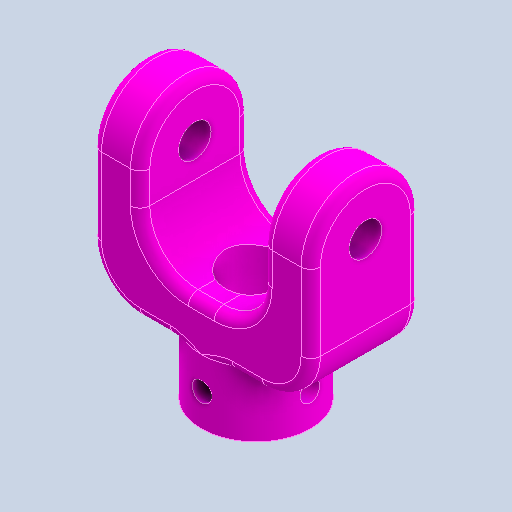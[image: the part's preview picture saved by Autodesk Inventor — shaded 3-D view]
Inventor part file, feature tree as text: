
AUTODESK INVENTOR PART (.ipt)
format: ipt  version: 2022 (Build 260153000, 153)  size: 330,752 bytes
history: native  units: in
note: dims shown in document units (in); Inventor stores cm internally (conversion verified against a paired STEP export)
features: extrude x5, sketch x5, fillet x4, plane x1, other x1, pattern_circular x1
ambient origin geometry x8: Origin, YZ Plane, XZ Plane, XY Plane, X Axis, Y Axis, Z Axis, Center Point
bodies: Solid1 (feature_tree)
feature tree (17):
  extrude  "Extrusion1"  Depth=2.6772in
  fillet  "Fillet1"  Radius=0.5906in
  fillet  "Fillet2"  Radius=0.5906in
  fillet  "Fillet3"  Radius=0.5512in
  extrude  "Extrusion2"  Depth=1.3386in TaperAngle=0.0deg
  extrude  "Extrusion3"  Depth=0.6693in
  fillet  "Fillet4"  Radius=0.5906in
  plane  "Work Plane1"
  extrude  "Extrusion4"  Depth=0.6693in
  other  "Work Axis1"
  pattern_circular  "Circular Pattern1"  Count=2  [1 undecoded]
  extrude  "Extrusion5"  Depth=0.3937in
  sketch  "Sketch1"  dims[d0=2.2047in d1=2.6772in d2=0.5906in d3=0.5906in d4=0.5512in]
  sketch  "Sketch2"  dims[d5=1.4961in d6=1.3386in d7=0.0in]
  sketch  "Sketch3"  dims[d8=0.6693in d9=0.6693in d10=0.5906in]
  sketch  "Sketch4"  dims[d11=1.3386in d12=0.6693in]
  sketch  "Sketch5"  dims[d13=1.3386in d14=0.7874in d15=0.0in d16=0.748in d17=0.0in d18=0.0in d19=0.1181in d20=0.6693in d21=0.2362in d22=0.3937in d23=0.6693in d24=0.0in d25=0.0in d26=1.5748in d27=360.0deg d29=0.3976in d30=0.6496in d31=0.6693in d32=0.0in d33=0.0in]
note: 1 required parameter value undecoded (feature->parameter linkage not recoverable at this tier; creation-order binding heuristic only, values carry confidence <= 0.55)
